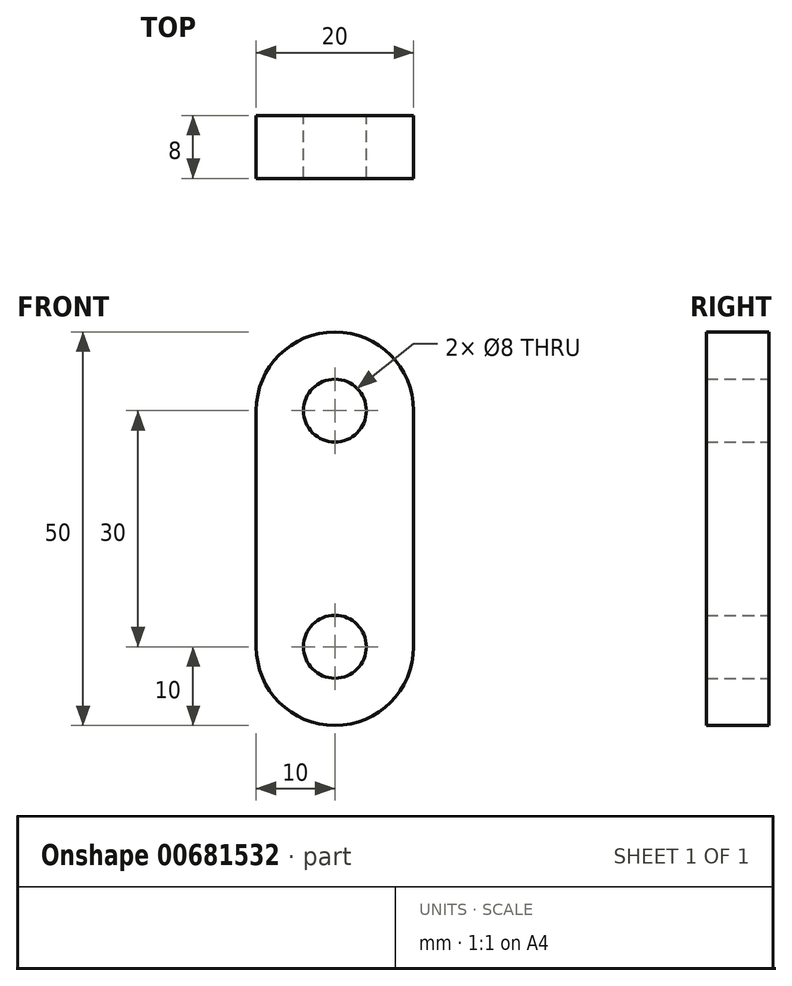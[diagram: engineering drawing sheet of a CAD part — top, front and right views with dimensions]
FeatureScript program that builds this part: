
annotation { "Feature Type Name" : "Feature", "Feature Type Description" : "" }
export const myFeature = defineFeature(function(context is Context, id is Id, definition is map)
    precondition{}
    {
        {
            var Q0;
            Q0=qCreatedBy(makeId("Front.planeOp"),FACE);
            var sketch = newSketch(context, id + "F0", { "sketchPlane" : qUnion([Q0])});
            skCircle(sketch, "E0", {"center": v(0, 0) * mm, "radius": 4 * mm});
            skCircle(sketch, "E1", {"center": v(0, 30) * mm, "radius": 4 * mm});
            skArc(sketch, "E2", {"start": v(10, 30) * mm, "mid": v(0, 40) * mm, "end": v(-10, 30) * mm});
            skArc(sketch, "E3", {"start": v(-10, 0) * mm, "mid": v(0, -10) * mm, "end": v(10, 0) * mm});
            skLineSegment(sketch, "E4", {"start": v(-10, 30) * mm, "end": v(-10, 0) * mm});
            skLineSegment(sketch, "E5", {"start": v(10, 0) * mm, "end": v(10, 30) * mm});
            skSolve(sketch);
        }
        {
            var Q0;
            Q0 = qSketchRegion(id + "F0", true);
            extrude(context, id + "F1", {"entities" : qUnion([Q0]), "endBound" : BoundingType.SYMMETRIC, "depth" : 8 * mm, "offsetDistance" : 25 * mm});
        }
    });
